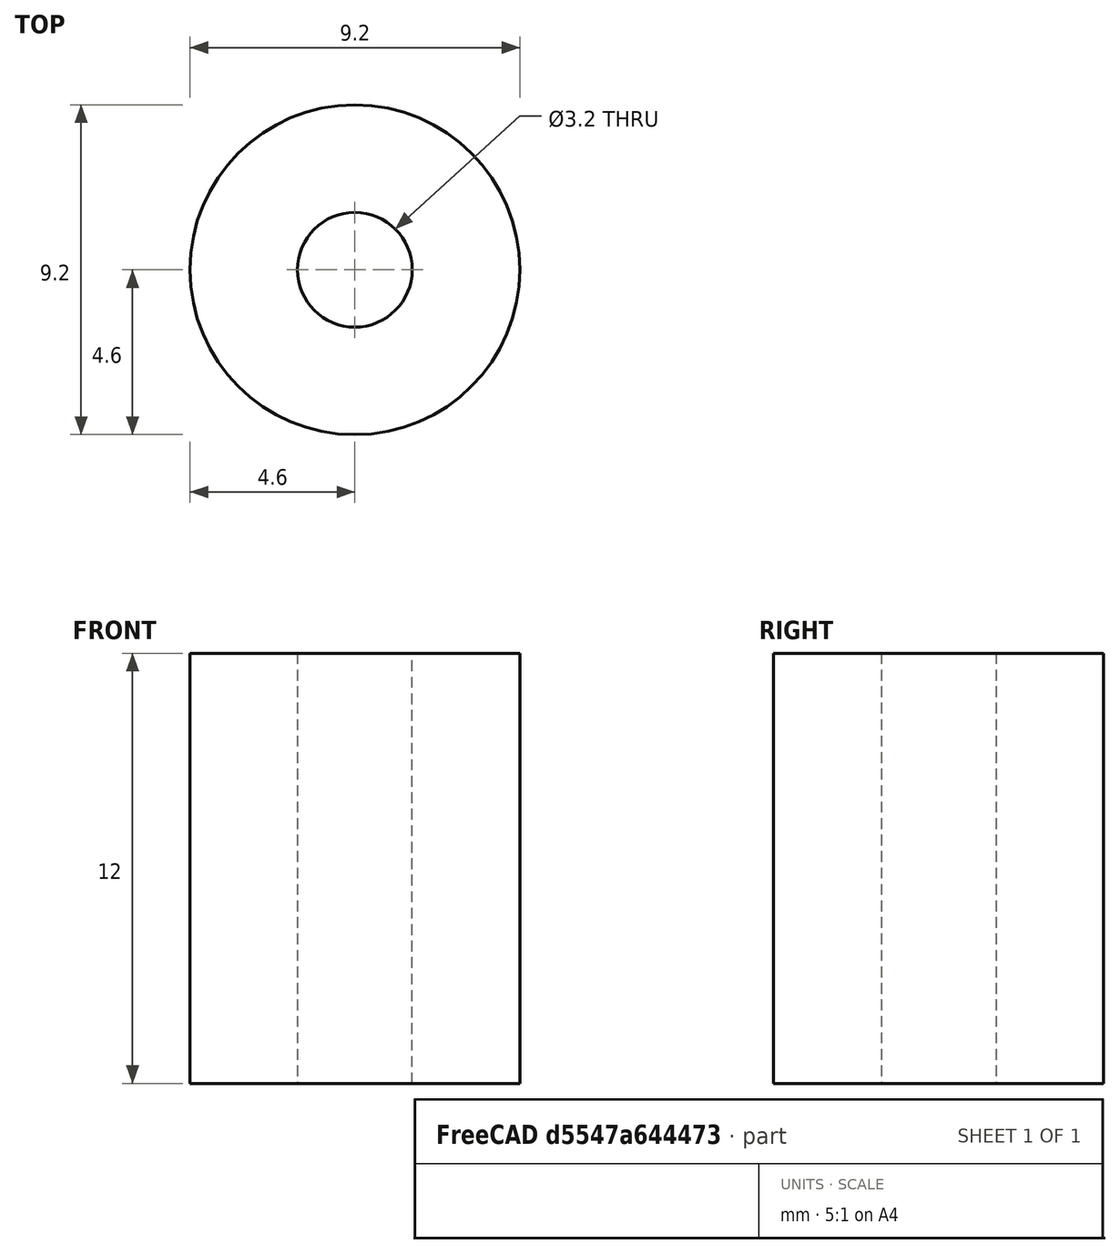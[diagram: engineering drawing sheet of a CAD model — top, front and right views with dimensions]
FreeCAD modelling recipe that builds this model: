
FCSTD DOCUMENT  (FreeCAD 1.0R39109 (Git))
Label: motorSpacer
License: All rights reserved
LicenseURL: https://en.wikipedia.org/wiki/All_rights_reserved
objects: Sketcher::SketchObject×1, PartDesign::Pad×1, PartDesign::Body×1
note: 6 computed .brp shape members not serialized (recipe doc carries the construction recipe); baked Part::Feature solids carry a one-line shape summary decoded from their .brp

FEATURE [Sketcher::SketchObject] Sketch
  ArcFitTolerance = 1e-06
  AttachmentSupport = -> [XY_Plane]
  FullyConstrained = true
  MakeInternals = false
  MapMode = 5
  sketch-geometry (2):
    g0: Circle CenterX=0 CenterY=0 CenterZ=0 NormalX=0 NormalY=0 NormalZ=1 AngleXU=0 Radius=1.6
    g1: Circle CenterX=0 CenterY=0 CenterZ=0 NormalX=0 NormalY=0 NormalZ=1 AngleXU=0 Radius=4.6
  constraints (4):
    c: Coincident(g0,g-1)
    c: Coincident(g1,g0)
    c: Diameter(g0) = 3.2
    c: Distance(g0,g1) = 3
FEATURE [PartDesign::Pad] Pad
  Direction = (0,0,1)
  Length = 12
  Length2 = 10
  Profile = -> Sketch
  ReferenceAxis = -> Sketch [N_Axis]
  Refine = true
  Suppressed = false
  Type = 0
FEATURE [PartDesign::Body] Body
  AllowCompound = false
  Group = -> [Sketch,Pad]
  Origin = -> Origin
  Tip = -> Pad
